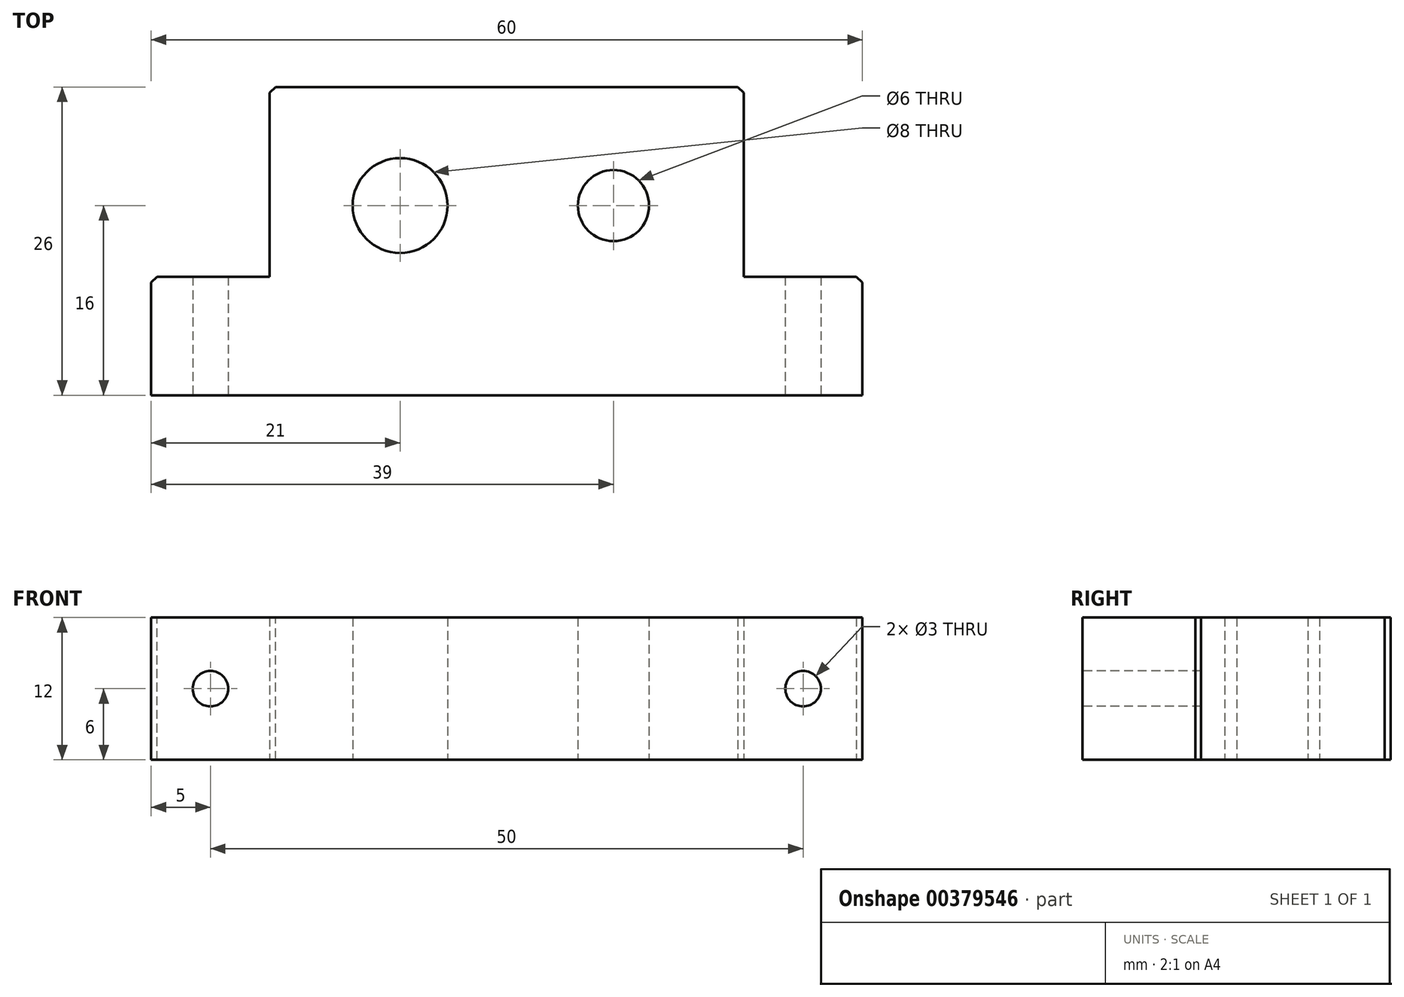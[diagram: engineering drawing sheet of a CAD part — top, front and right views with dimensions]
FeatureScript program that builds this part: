
annotation { "Feature Type Name" : "Feature", "Feature Type Description" : "" }
export const myFeature = defineFeature(function(context is Context, id is Id, definition is map)
    precondition{}
    {
        {
            var Q0;
            Q0=qCreatedBy(makeId("Top.planeOp"),FACE);
            var sketch = newSketch(context, id + "F0", { "sketchPlane" : qUnion([Q0])});
            skLineSegment(sketch, "E0", {"start": v(-30, 0) * mm, "end": v(30, 0) * mm});
            skLineSegment(sketch, "E1", {"start": v(30, 0) * mm, "end": v(30, 10) * mm});
            skLineSegment(sketch, "E2", {"start": v(30, 10) * mm, "end": v(20, 10) * mm});
            skLineSegment(sketch, "E3", {"start": v(20, 10) * mm, "end": v(20, 26) * mm});
            skLineSegment(sketch, "E4", {"start": v(20, 26) * mm, "end": v(-20, 26) * mm});
            skLineSegment(sketch, "E5", {"start": v(-20, 26) * mm, "end": v(-20, 10) * mm});
            skLineSegment(sketch, "E6", {"start": v(-20, 10) * mm, "end": v(-30, 10) * mm});
            skLineSegment(sketch, "E7", {"start": v(-30, 10) * mm, "end": v(-30, 0) * mm});
            skPoint(sketch, "E8.orphan", {"position": v(-30, 0) * mm});
            skLineSegment(sketch, "E9", {"start": v(0, 0) * mm, "end": v(0, 48.17) * mm, "construction": true});
            skCircle(sketch, "E10", {"center": v(9, 16) * mm, "radius": 3 * mm});
            skCircle(sketch, "E11", {"center": v(-9, 16) * mm, "radius": 4 * mm});
            skSolve(sketch);
        }
        {
            var Q0;
            Q0 = qSketchRegion(id + "F0", true);
            extrude(context, id + "F1", {"entities" : qUnion([Q0]), "depth" : 6 * mm, "hasSecondDirection" : true, "secondDirectionOppositeDirection" : true, "secondDirectionDepth" : 6 * mm});
        }
        {
            var Q0;
            Q0=makeQuery(id+"F1.opExtrude","SWEPT_FACE",FACE,{"disambiguationData":[OSD([sQuery(id+"F0.wireOp",EDGE,"E0")])]});
            var sketch = newSketch(context, id + "F2", { "sketchPlane" : qUnion([Q0])});
            skCircle(sketch, "E12", {"center": v(-25, 0) * mm, "radius": 1.5 * mm});
            skPoint(sketch, "E12.centerSnap0", {"position": v(-30, 0) * mm});
            skCircle(sketch, "E13", {"center": v(25, 0) * mm, "radius": 1.5 * mm});
            skPoint(sketch, "E13.centerSnap0", {"position": v(30, 0) * mm});
            skSolve(sketch);
        }
        {
            var Q0;
            Q0 = qSketchRegion(id + "F2", true);
            extrude(context, id + "F3", {"entities" : qUnion([Q0]), "operationType" : NewBodyOperationType.REMOVE, "endBound" : BoundingType.THROUGH_ALL, "oppositeDirection" : true, "depth" : 25 * mm});
        }
        {
            var Q0;
            Q0=makeQuery(id+"F1.opExtrude","SWEPT_EDGE",EDGE,{"disambiguationData":[OSD([sQuery(id+"F0.wireOp",EDGE,"E4"),sQuery(id+"F0.wireOp",EDGE,"E5")])]});
            var Q1;
            Q1=makeQuery(id+"F1.opExtrude","SWEPT_EDGE",EDGE,{"disambiguationData":[OSD([sQuery(id+"F0.wireOp",EDGE,"E3"),sQuery(id+"F0.wireOp",EDGE,"E4")])]});
            var Q2;
            Q2=makeQuery(id+"F1.opExtrude","SWEPT_EDGE",EDGE,{"disambiguationData":[OSD([sQuery(id+"F0.wireOp",EDGE,"E1"),sQuery(id+"F0.wireOp",EDGE,"E2")])]});
            var Q3;
            Q3=makeQuery(id+"F1.opExtrude","SWEPT_EDGE",EDGE,{"disambiguationData":[OSD([sQuery(id+"F0.wireOp",EDGE,"E6"),sQuery(id+"F0.wireOp",EDGE,"E7")])]});
            chamfer(context, id + "F4", {"entities" : qUnion([Q0, Q1, Q2, Q3]), "width" : .5 * mm, "tangentPropagation" : true});
        }
    });
